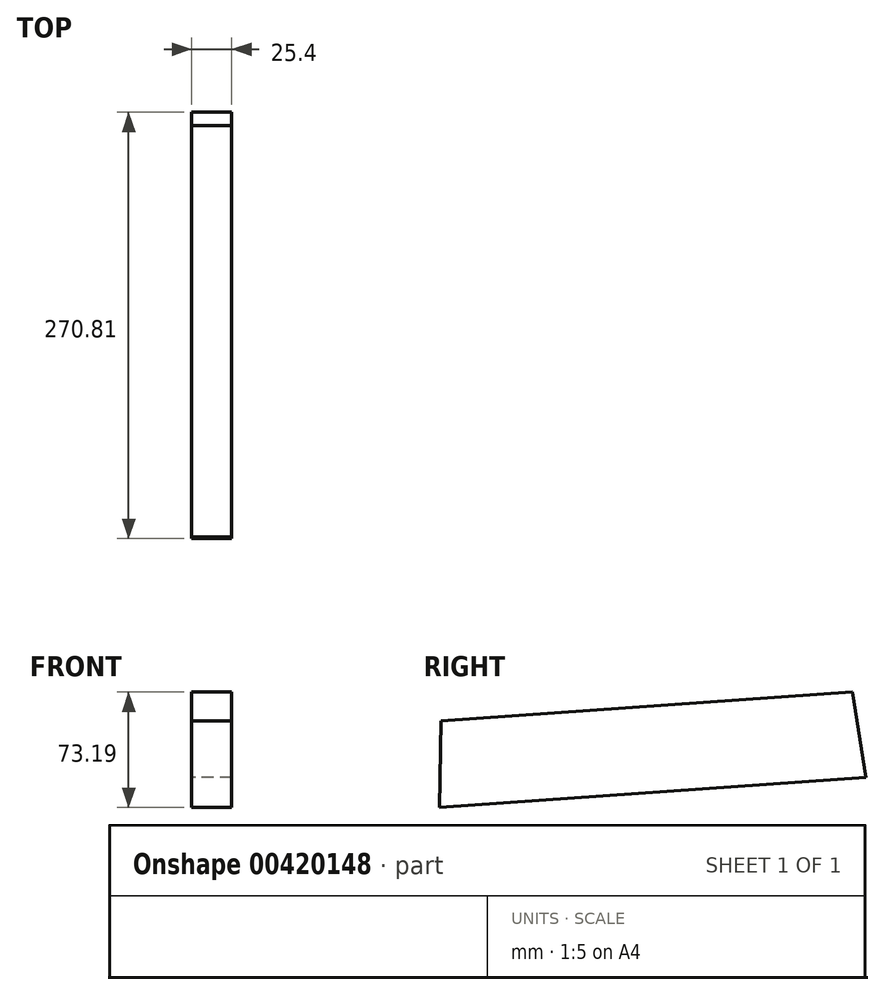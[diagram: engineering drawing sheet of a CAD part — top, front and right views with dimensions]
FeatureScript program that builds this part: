
annotation { "Feature Type Name" : "Feature", "Feature Type Description" : "" }
export const myFeature = defineFeature(function(context is Context, id is Id, definition is map)
    precondition{}
    {
        {
            var Q0;
            Q0=qCreatedBy(makeId("Right.planeOp"),FACE);
            var sketch = newSketch(context, id + "F0", { "sketchPlane" : qUnion([Q0])});
            skLineSegment(sketch, "E0", {"start": v(128.89, 34.12) * mm, "end": v(137.48, -20.17) * mm});
            skLineSegment(sketch, "E1", {"start": v(137.48, -20.17) * mm, "end": v(-133.33, -39.07) * mm});
            skLineSegment(sketch, "E2", {"start": v(-133.33, -39.07) * mm, "end": v(-132.36, 15.9) * mm});
            skLineSegment(sketch, "E3", {"start": v(-132.36, 15.9) * mm, "end": v(128.89, 34.12) * mm});
            skLineSegment(sketch, "E4", {"start": v(-133.33, -39.07) * mm, "end": v(-138.3, 32.14) * mm, "construction": true});
            skLineSegment(sketch, "E5", {"start": v(137.48, -20.17) * mm, "end": v(132.35, 53.26) * mm, "construction": true});
            skSolve(sketch);
        }
        {
            var Q0;
            Q0=makeQuery(id+"F0.imprint","IMPRINT",FACE,{"disambiguationData":[TD([[makeQuery(id+"F0.imprint","IMPRINT",EDGE,{"derivedFrom":sQuery(id+"F0.wireOp",EDGE,"E0")}),-1.0]])]});
            extrude(context, id + "F1", {"entities" : qUnion([Q0]), "depth" : 25.4 * mm});
        }
    });
